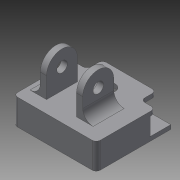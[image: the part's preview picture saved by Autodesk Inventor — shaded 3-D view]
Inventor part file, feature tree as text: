
AUTODESK INVENTOR PART (.ipt)
format: ipt  version: 2013 (Build 170138000, 138)  size: 210,432 bytes
history: native  units: mm
features: extrude x8, sketch x8, fillet x3, mirror x2
ambient origin geometry x8: Origin, YZ Plane, XZ Plane, XY Plane, X Axis, Y Axis, Z Axis, Center Point
bodies: Solid1 (feature_tree)
feature tree (21):
  extrude  "Extrusion1"  Depth=6.35mm
  extrude  "Extrusion2"  Depth=10.0mm
  extrude  "Extrusion3"  Depth=8.5mm TaperAngle=0.0deg
  mirror  "Mirror1"
  extrude  "Extrusion4"  Depth=2.0mm TaperAngle=0.0deg
  mirror  "Mirror2"
  extrude  "Extrusion5"  Depth=2.0mm TaperAngle=0.0deg
  extrude  "Extrusion6"  Depth=12.5mm
  extrude  "Extrusion7"  Depth=12.5mm
  fillet  "Fillet1"  Radius=16.0mm
  fillet  "Fillet2"  Radius=15.0mm
  fillet  "Fillet3"  Radius=3.0mm
  extrude  "Extrusion8"  Depth=14.5mm
  sketch  "Sketch1"  dims[d0=40.0mm d2=6.35mm]
  sketch  "Sketch2"  dims[d4=9.5mm d5=10.0mm]
  sketch  "Sketch4"  dims[d6=20.0mm d7=8.5mm d8=0.0mm]
  sketch  "Sketch5"  dims[d9=20.0mm d10=2.0mm d11=0.0mm]
  sketch  "Sketch6"  dims[d12=6.35mm d13=2.0mm d14=0.0mm]
  sketch  "Sketch7"  dims[d15=7.0mm d17=12.5mm]
  sketch  "Sketch8"  dims[d18=2.0mm d19=0.0mm d20=12.5mm d21=16.0mm d22=0.0mm d23=15.0mm d25=3.0mm]
  sketch  "Sketch9"  dims[d27=5.0mm d28=14.5mm d29=17.5mm d30=0.0mm d31=5.1mm d34=7.5mm d35=10.0mm d36=0.0mm d37=7.5mm d38=4.5mm d39=5.0mm d40=2.0mm d41=2.0mm d42=13.5mm d43=4.0mm d44=0.0mm]
